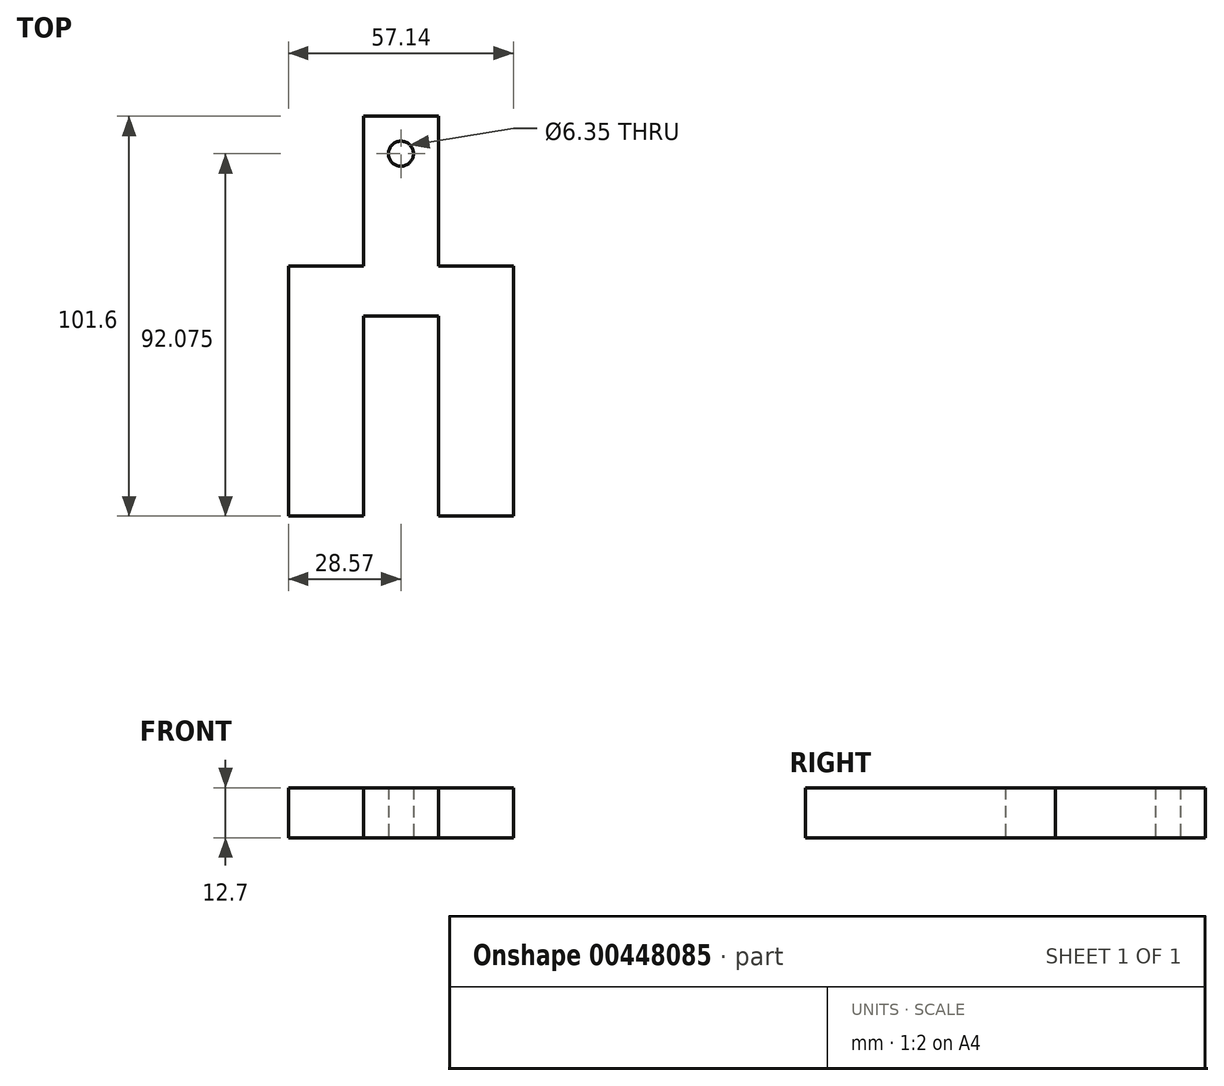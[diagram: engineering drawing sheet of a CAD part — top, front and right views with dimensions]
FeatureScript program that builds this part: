
annotation { "Feature Type Name" : "Feature", "Feature Type Description" : "" }
export const myFeature = defineFeature(function(context is Context, id is Id, definition is map)
    precondition{}
    {
        {
            var Q0;
            Q0=qCreatedBy(makeId("Top.planeOp"),FACE);
            var sketch = newSketch(context, id + "F0", { "sketchPlane" : qUnion([Q0])});
            skLineSegment(sketch, "E0.bottom", {"start": v(-9.52, 50.8) * mm, "end": v(9.53, 50.8) * mm});
            skLineSegment(sketch, "E0.top", {"start": v(-9.53, -50.8) * mm, "end": v(9.53, -50.8) * mm});
            skLineSegment(sketch, "E0.left", {"start": v(-9.52, 50.8) * mm, "end": v(-9.53, -50.8) * mm});
            skLineSegment(sketch, "E0.right", {"start": v(9.53, 50.8) * mm, "end": v(9.53, -50.8) * mm});
            skPoint(sketch, "E0.middle", {"position": v(0, 0) * mm});
            skCircle(sketch, "E1", {"center": v(0, 41.28) * mm, "radius": 3.18 * mm});
            skPoint(sketch, "E2.oppositeSnap0", {"position": v(9.53, 0) * mm});
            skLineSegment(sketch, "E2.bottom", {"start": v(9.53, -50.8) * mm, "end": v(28.57, -50.8) * mm});
            skLineSegment(sketch, "E2.top", {"start": v(9.53, 0) * mm, "end": v(28.57, 0) * mm});
            skLineSegment(sketch, "E2.left", {"start": v(9.53, -50.8) * mm, "end": v(9.53, 0) * mm});
            skLineSegment(sketch, "E2.right", {"start": v(28.57, -50.8) * mm, "end": v(28.57, 0) * mm});
            skLineSegment(sketch, "E3.MirrorCS", {"start": v(-9.53, 0) * mm, "end": v(-28.57, 0) * mm});
            skLineSegment(sketch, "E4.MirrorCS", {"start": v(-9.53, -50.8) * mm, "end": v(-28.57, -50.8) * mm});
            skLineSegment(sketch, "E5.MirrorCS", {"start": v(-28.57, -50.8) * mm, "end": v(-28.57, 0) * mm});
            skLineSegment(sketch, "E6.bottom", {"start": v(-28.57, 0) * mm, "end": v(28.57, 0) * mm});
            skLineSegment(sketch, "E6.top", {"start": v(-28.57, 12.7) * mm, "end": v(28.57, 12.7) * mm});
            skLineSegment(sketch, "E6.left", {"start": v(-28.57, 0) * mm, "end": v(-28.57, 12.7) * mm});
            skLineSegment(sketch, "E6.right", {"start": v(28.57, 0) * mm, "end": v(28.57, 12.7) * mm});
            skSolve(sketch);
        }
        {
            var Q0;
            {var subQ1=sQuery(id+"F0.wireOp",EDGE,"E0.bottom");Q0=makeQuery(id+"F0.imprint","IMPRINT",FACE,{"disambiguationData":[TD([[makeQuery(id+"F0.imprint","IMPRINT",EDGE,{"derivedFrom":subQ1}),-1.0]])]});}
            var Q1;
            {var subQ5=sQuery(id+"F0.wireOp",EDGE,"E6.left");Q1=makeQuery(id+"F0.imprint","IMPRINT",FACE,{"disambiguationData":[TD([[makeQuery(id+"F0.imprint","IMPRINT",EDGE,{"derivedFrom":subQ5}),-1.0]])]});}
            var Q2;
            {var subQ0=sQuery(id+"F0.wireOp",EDGE,"E4.MirrorCS");Q2=makeQuery(id+"F0.imprint","IMPRINT",FACE,{"disambiguationData":[TD([[makeQuery(id+"F0.imprint","IMPRINT",EDGE,{"derivedFrom":subQ0}),-1.0]])]});}
            var Q3;
            {var subQ5=sQuery(id+"F0.wireOp",EDGE,"E6.right");Q3=makeQuery(id+"F0.imprint","IMPRINT",FACE,{"disambiguationData":[TD([[makeQuery(id+"F0.imprint","IMPRINT",EDGE,{"derivedFrom":subQ5}),1.0]])]});}
            var Q4;
            Q4=makeQuery(id+"F0.imprint","IMPRINT",FACE,{"disambiguationData":[TD([[makeQuery(id+"F0.imprint","IMPRINT",EDGE,{"derivedFrom":sQuery(id+"F0.wireOp",EDGE,"E2.bottom")}),1.0]])]});
            var Q5;
            {var subQ0=sQuery(id+"F0.wireOp",EDGE,"E6.top");var subQ1=sQuery(id+"F0.wireOp",EDGE,"E0.left");var subQ2=makeQuery(id+"F0.imprint","INTERSECT",VERTEX,{"derivedFrom":[subQ1,subQ0]});Q5=makeQuery(id+"F0.imprint","IMPRINT",FACE,{"disambiguationData":[TD([[makeQuery(id+"F0.imprint","IMPRINT",EDGE,{"disambiguationData":[TD([[subQ2,-1.0]])],"derivedFrom":subQ1}),1.0]])]});}
            extrude(context, id + "F1", {"entities" : qUnion([Q0, Q1, Q2, Q3, Q4, Q5]), "depth" : 12.7 * mm});
        }
    });
